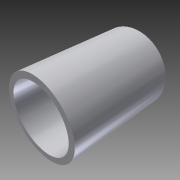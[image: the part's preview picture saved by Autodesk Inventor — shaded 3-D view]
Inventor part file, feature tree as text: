
AUTODESK INVENTOR PART (.ipt)
format: ipt  version: 2013 (Build 170138000, 138)  size: 84,480 bytes
history: native  units: in
note: dims shown in document units (in); Inventor stores cm internally (conversion verified against a paired STEP export)
features: extrude x1, sketch x1
ambient origin geometry x8: Origin, YZ Plane, XZ Plane, XY Plane, X Axis, Y Axis, Z Axis, Center Point
bodies: Solid1 (feature_tree)
feature tree (2):
  extrude  "Extrusion1"  Depth=2.0in
  sketch  "Sketch1"  dims[d0=2.375in d2=2.0in d3=3.25in d4=0.0in]
